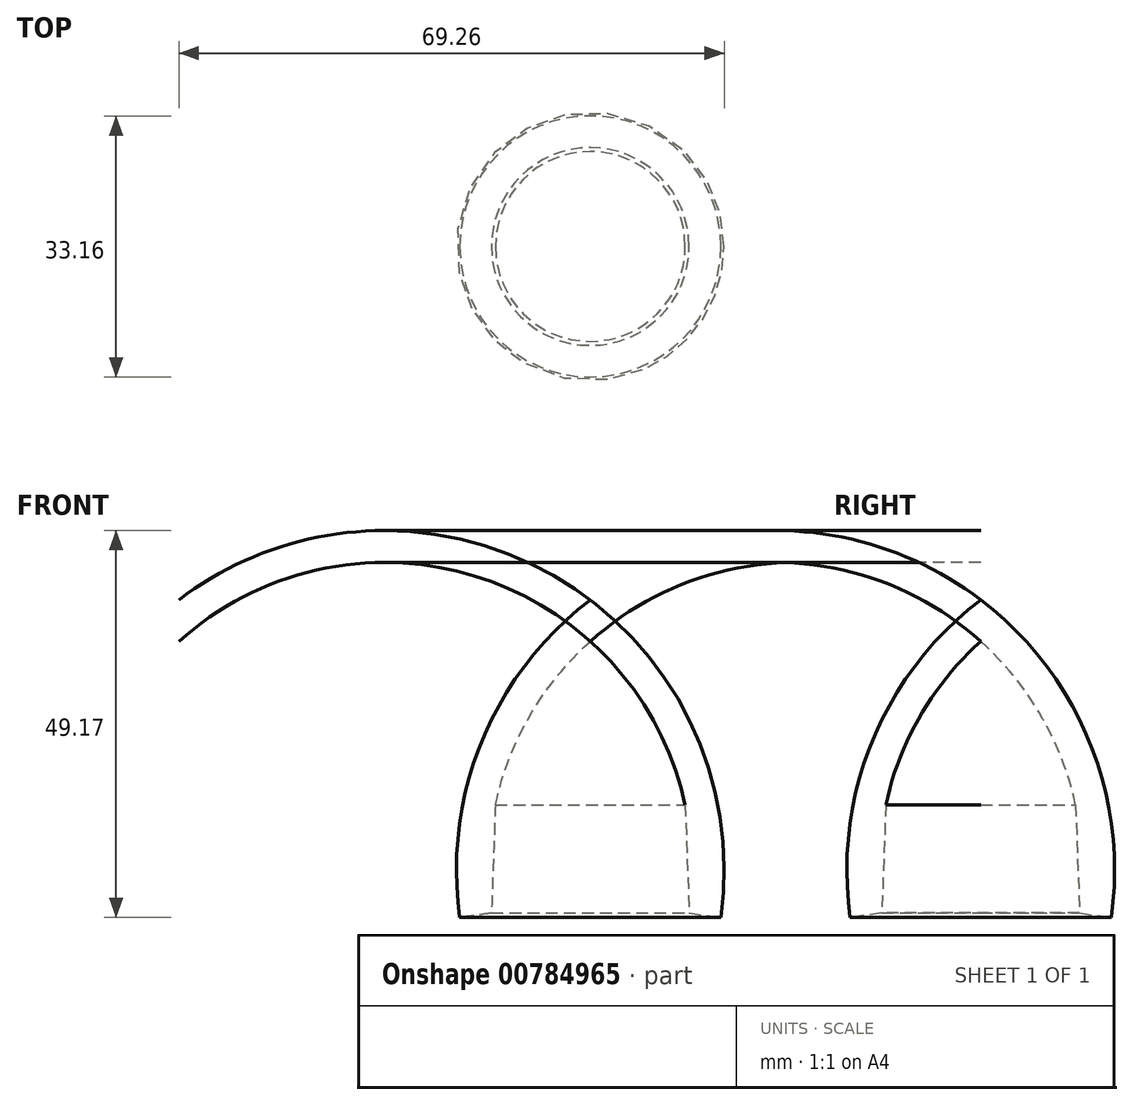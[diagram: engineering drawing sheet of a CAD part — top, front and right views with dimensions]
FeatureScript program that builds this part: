
annotation { "Feature Type Name" : "Feature", "Feature Type Description" : "" }
export const myFeature = defineFeature(function(context is Context, id is Id, definition is map)
    precondition{}
    {
        {
            var Q0;
            Q0=qCreatedBy(makeId("Front.planeOp"),FACE);
            var sketch = newSketch(context, id + "F0", { "sketchPlane" : qUnion([Q0])});
            skLineSegment(sketch, "E0", {"start": v(0, 35.08) * mm, "end": v(0, 40.35) * mm});
            skArc(sketch, "E1", {"start": v(16.58, 0) * mm, "mid": v(13.77, 22.43) * mm, "end": v(0, 40.35) * mm});
            skArc(sketch, "E2.0", {"start": v(12.06, 14.32) * mm, "mid": v(7.66, 25.65) * mm, "end": v(0, 35.08) * mm});
            skLineSegment(sketch, "E3", {"start": v(12.06, 14.32) * mm, "end": v(12.56, 0.57) * mm});
            skLineSegment(sketch, "E4", {"start": v(12.56, 0.57) * mm, "end": v(16.58, 0) * mm});
            skSolve(sketch);
        }
        {
            var Q0;
            Q0 = qSketchRegion(id + "F0", true);
            var Q1;
            Q1=sQuery(id+"F0.wireOp",EDGE,"E0");
            revolve(context, id + "F1", {"surfaceOperationType" : NewSurfaceOperationType.NEW, "entities" : qUnion([Q0]), "axis" : qUnion([Q1]), "revolveType" : RevolveType.FULL});
        }
    });
